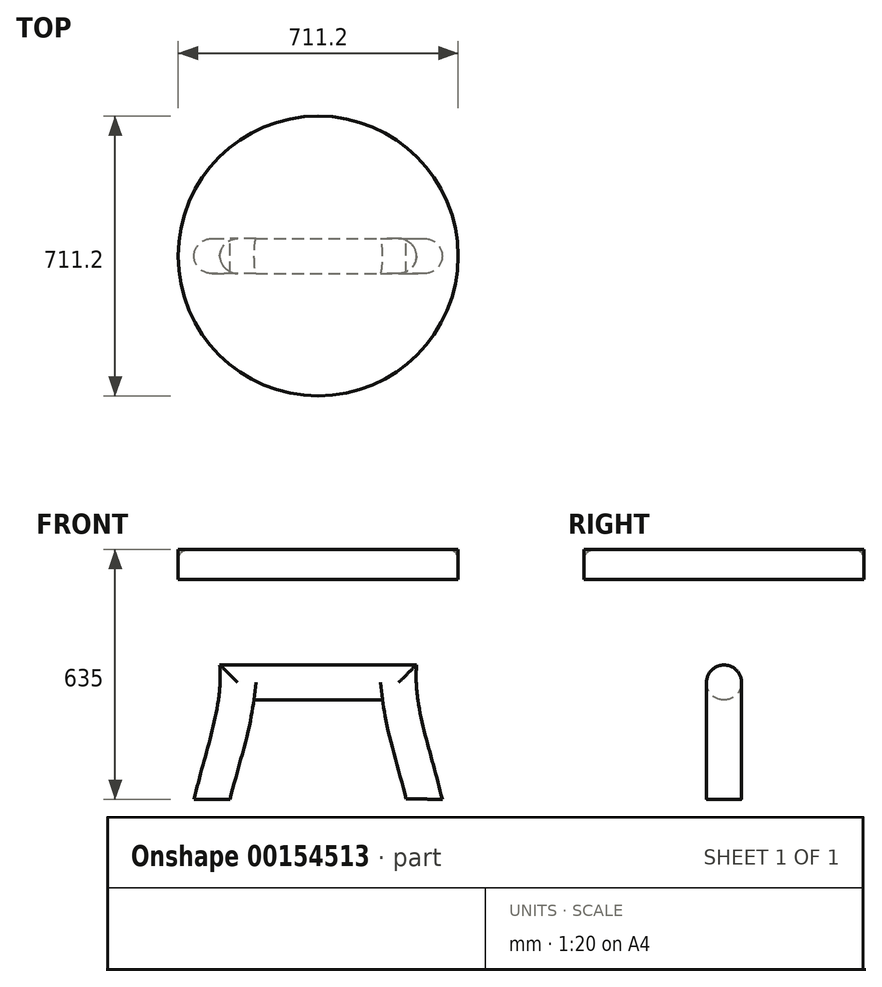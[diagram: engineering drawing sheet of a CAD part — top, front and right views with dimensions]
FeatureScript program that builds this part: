
annotation { "Feature Type Name" : "Feature", "Feature Type Description" : "" }
export const myFeature = defineFeature(function(context is Context, id is Id, definition is map)
    precondition{}
    {
        {
            var Q0;
            Q0=qCreatedBy(makeId("Top.planeOp"),FACE);
            var sketch = newSketch(context, id + "F0", { "sketchPlane" : qUnion([Q0])});
            skCircle(sketch, "E0", {"center": v(0, 0) * mm, "radius": 355.6 * mm});
            skSolve(sketch);
        }
        {
            var Q0;
            Q0=makeQuery(id+"F0.imprint","IMPRINT",FACE,{"disambiguationData":[TD([[makeQuery(id+"F0.imprint","IMPRINT",EDGE,{"derivedFrom":sQuery(id+"F0.wireOp",EDGE,"E0")}),1.0]])]});
            extrude(context, id + "F1", {"entities" : qUnion([Q0]), "oppositeDirection" : true, "depth" : 76.2 * mm});
        }
        {
            var Q0;
            Q0=qCreatedBy(makeId("Front.planeOp"),FACE);
            var sketch = newSketch(context, id + "F2", { "sketchPlane" : qUnion([Q0])});
            skFitSpline(sketch, "E1", {"points": [v(-350.08, -37.61) * mm, v(-250, -293.53) * mm, v(-315.3, -635) * mm], "startDerivative": vector(306.3, -378.15) * mm, "endDerivative": vector(-196.23, -818.74) * mm});
            skLineSegment(sketch, "E2", {"start": v(-315.3, -635) * mm, "end": v(-223.77, -635) * mm});
            skFitSpline(sketch, "E3.0", {"points": [v(-281, 18.35) * mm, v(-276.82, 13.2) * mm, v(-268.7, 2.6) * mm, v(-257.06, -14.11) * mm, v(-245.96, -31.62) * mm, v(-231.83, -55.95) * mm, v(-215.44, -88.12) * mm, v(-200.93, -122.28) * mm, v(-190.63, -150.57) * mm, v(-183.6, -172.21) * mm, v(-177.33, -194.23) * mm, v(-171.89, -216.57) * mm, v(-168.1, -235.43) * mm, v(-165.57, -250.63) * mm, v(-163.92, -262.08) * mm, v(-162.77, -271.67) * mm, v(-162, -279.36) * mm, v(-161.48, -285.15) * mm, v(-161.04, -290.93) * mm, v(-160.68, -296.7) * mm, v(-160.4, -302.43) * mm, v(-160.12, -310.05) * mm, v(-159.94, -319.52) * mm, v(-160.02, -330.79) * mm, v(-160.35, -341.95) * mm, v(-161.14, -356.72) * mm, v(-162.7, -374.92) * mm, v(-165.43, -396.41) * mm, v(-168.87, -417.58) * mm, v(-174.27, -445.47) * mm, v(-182.29, -479.9) * mm, v(-193.22, -521.32) * mm, v(-204.93, -563.73) * mm, v(-216.97, -608.02) * mm, v(-224.94, -639.41) * mm, v(-228.85, -655.72) * mm]});
            skLineSegment(sketch, "E4", {"start": v(0, 0) * mm, "end": v(0, -373.88) * mm, "construction": true});
            skFitSpline(sketch, "E5.MirrorCS", {"points": [v(350.08, -37.61) * mm, v(250, -293.53) * mm, v(315.3, -635) * mm], "startDerivative": vector(-306.3, -378.15) * mm, "endDerivative": vector(196.23, -818.74) * mm});
            skFitSpline(sketch, "E6.0", {"points": [v(281, 18.35) * mm, v(276.82, 13.2) * mm, v(268.7, 2.6) * mm, v(257.06, -14.11) * mm, v(245.96, -31.62) * mm, v(231.83, -55.95) * mm, v(215.44, -88.12) * mm, v(200.93, -122.28) * mm, v(190.63, -150.57) * mm, v(183.6, -172.21) * mm, v(177.33, -194.23) * mm, v(171.89, -216.57) * mm, v(168.1, -235.43) * mm, v(165.57, -250.63) * mm, v(163.92, -262.08) * mm, v(162.77, -271.67) * mm, v(162, -279.36) * mm, v(161.48, -285.15) * mm, v(161.04, -290.93) * mm, v(160.68, -296.7) * mm, v(160.4, -302.43) * mm, v(160.12, -310.05) * mm, v(159.94, -319.52) * mm, v(160.02, -330.79) * mm, v(160.35, -341.95) * mm, v(161.14, -356.72) * mm, v(162.7, -374.92) * mm, v(165.43, -396.41) * mm, v(168.87, -417.58) * mm, v(174.27, -445.47) * mm, v(182.29, -479.9) * mm, v(193.22, -521.32) * mm, v(204.93, -563.73) * mm, v(216.97, -608.02) * mm, v(224.94, -639.41) * mm, v(228.85, -655.72) * mm]});
            skLineSegment(sketch, "E7", {"start": v(-350.08, -37.61) * mm, "end": v(-242.53, -37.61) * mm});
            skLineSegment(sketch, "E8", {"start": v(350.08, -37.61) * mm, "end": v(242.53, -37.61) * mm});
            skLineSegment(sketch, "E9", {"start": v(250, -293.53) * mm, "end": v(-250, -293.53) * mm});
            skLineSegment(sketch, "E10", {"start": v(253.36, -382.43) * mm, "end": v(-253.36, -382.43) * mm});
            skLineSegment(sketch, "E11", {"start": v(223.32, -633.2) * mm, "end": v(315.3, -635) * mm});
            skSolve(sketch);
        }
        {
            var Q0;
            {var subQ0=sQuery(id+"F2.wireOp",EDGE,"E7");var subQ1=sQuery(id+"F2.wireOp",EDGE,"E1");var subQ2=makeQuery(id+"F2.imprint","INTERSECT",VERTEX,{"derivedFrom":[subQ1,subQ0]});Q0=makeQuery(id+"F2.imprint","IMPRINT",FACE,{"disambiguationData":[TD([[makeQuery(id+"F2.imprint","IMPRINT",EDGE,{"disambiguationData":[TD([[subQ2,-1.0]])],"derivedFrom":subQ1}),1.0]])]});}
            var Q1;
            {var subQ0=sQuery(id+"F2.wireOp",EDGE,"E9");var subQ1=sQuery(id+"F2.wireOp",EDGE,"E1");var subQ2=makeQuery(id+"F2.imprint","INTERSECT",VERTEX,{"derivedFrom":[subQ1,subQ0]});Q1=makeQuery(id+"F2.imprint","IMPRINT",FACE,{"disambiguationData":[TD([[makeQuery(id+"F2.imprint","IMPRINT",EDGE,{"disambiguationData":[TD([[subQ2,-1.0]])],"derivedFrom":subQ1}),1.0]])]});}
            var Q2;
            {var subQ0=sQuery(id+"F2.wireOp",EDGE,"E10");var subQ1=sQuery(id+"F2.wireOp",EDGE,"E3.0");var subQ2=makeQuery(id+"F2.imprint","INTERSECT",VERTEX,{"derivedFrom":[subQ1,subQ0]});Q2=makeQuery(id+"F2.imprint","IMPRINT",FACE,{"disambiguationData":[TD([[makeQuery(id+"F2.imprint","IMPRINT",EDGE,{"disambiguationData":[TD([[subQ2,1.0]])],"derivedFrom":subQ1}),1.0]])]});}
            var Q3;
            {var subQ0=sQuery(id+"F2.wireOp",EDGE,"E8");var subQ1=sQuery(id+"F2.wireOp",EDGE,"E5.MirrorCS");var subQ2=makeQuery(id+"F2.imprint","INTERSECT",VERTEX,{"derivedFrom":[subQ1,subQ0]});Q3=makeQuery(id+"F2.imprint","IMPRINT",FACE,{"disambiguationData":[TD([[makeQuery(id+"F2.imprint","IMPRINT",EDGE,{"disambiguationData":[TD([[subQ2,-1.0]])],"derivedFrom":subQ1}),-1.0]])]});}
            var Q4;
            {var subQ0=sQuery(id+"F2.wireOp",EDGE,"E9");var subQ1=sQuery(id+"F2.wireOp",EDGE,"E5.MirrorCS");var subQ2=makeQuery(id+"F2.imprint","INTERSECT",VERTEX,{"derivedFrom":[subQ1,subQ0]});Q4=makeQuery(id+"F2.imprint","IMPRINT",FACE,{"disambiguationData":[TD([[makeQuery(id+"F2.imprint","IMPRINT",EDGE,{"disambiguationData":[TD([[subQ2,-1.0]])],"derivedFrom":subQ1}),-1.0]])]});}
            var Q5;
            {var subQ0=sQuery(id+"F2.wireOp",EDGE,"E2");Q5=makeQuery(id+"F2.imprint","IMPRINT",FACE,{"disambiguationData":[TD([[makeQuery(id+"F2.imprint","IMPRINT",EDGE,{"derivedFrom":subQ0}),1.0]])]});}
            var Q6;
            {var subQ0=sQuery(id+"F2.wireOp",EDGE,"E11");var subQ1=sQuery(id+"F2.wireOp",EDGE,"E5.MirrorCS");var subQ2=makeQuery(id+"F2.imprint","INTERSECT",VERTEX,{"derivedFrom":[subQ1,subQ0]});Q6=makeQuery(id+"F2.imprint","IMPRINT",FACE,{"disambiguationData":[TD([[makeQuery(id+"F2.imprint","IMPRINT",EDGE,{"disambiguationData":[TD([[subQ2,1.0]])],"derivedFrom":subQ1}),-1.0]])]});}
            extrude(context, id + "F3", {"entities" : qUnion([Q0, Q1, Q2, Q3, Q4, Q5, Q6]), "operationType" : NewBodyOperationType.ADD, "depth" : 88.9 * mm, "symmetric" : true});
        }
        {
            var Q0;
            Q0=makeQuery(id+"F1.opExtrude","SWEPT_BODY",BODY,{"disambiguationData":[OSD([sQuery(id+"F0.wireOp",EDGE,"E0")])]});
            var Q1;
            Q1=makeQuery(id+"F1.opExtrude","CAP_EDGE",EDGE,{"disambiguationData":[OSD([sQuery(id+"F0.wireOp",EDGE,"E0")])],"isStart":true});
            circularPattern(context, id + "F4", {"operationType" : NewBodyOperationType.ADD, "entities" : qUnion([Q0]), "axis" : qUnion([Q1]), "angle" : 90 * degree, "instanceCount" : 2});
        }
        {
            var Q0;
            Q0=makeQuery(id+"F4.opPattern","COPY",EDGE,{"derivedFrom":makeQuery(id+"F3.opExtrude","CAP_EDGE",EDGE,{"disambiguationData":[OSD([sQuery(id+"F2.wireOp",EDGE,"E1")])],"isStart":false}),"instanceName":"1"});
            var Q1;
            Q1=makeQuery(id+"F4.opPattern","COPY",EDGE,{"derivedFrom":makeQuery(id+"F3.opExtrude","CAP_EDGE",EDGE,{"disambiguationData":[OSD([sQuery(id+"F2.wireOp",EDGE,"E1")])],"isStart":true}),"instanceName":"1"});
            var Q2;
            Q2=makeQuery(id+"F3.opExtrude","CAP_EDGE",EDGE,{"disambiguationData":[OSD([sQuery(id+"F2.wireOp",EDGE,"E5.MirrorCS")])],"isStart":false});
            var Q3;
            Q3=makeQuery(id+"F3.opExtrude","CAP_EDGE",EDGE,{"disambiguationData":[OSD([sQuery(id+"F2.wireOp",EDGE,"E5.MirrorCS")])],"isStart":true});
            var Q4;
            Q4=makeQuery(id+"F3.opExtrude","CAP_EDGE",EDGE,{"disambiguationData":[OSD([sQuery(id+"F2.wireOp",EDGE,"E1")])],"isStart":false});
            var Q5;
            Q5=makeQuery(id+"F3.opExtrude","CAP_EDGE",EDGE,{"disambiguationData":[OSD([sQuery(id+"F2.wireOp",EDGE,"E1")])],"isStart":true});
            var Q6;
            Q6=makeQuery(id+"F4.opPattern","COPY",EDGE,{"derivedFrom":makeQuery(id+"F3.opExtrude","CAP_EDGE",EDGE,{"disambiguationData":[OSD([sQuery(id+"F2.wireOp",EDGE,"E5.MirrorCS")])],"isStart":true}),"instanceName":"1"});
            var Q7;
            Q7=makeQuery(id+"F4.opPattern","COPY",EDGE,{"derivedFrom":makeQuery(id+"F3.opExtrude","CAP_EDGE",EDGE,{"disambiguationData":[OSD([sQuery(id+"F2.wireOp",EDGE,"E5.MirrorCS")])],"isStart":false}),"instanceName":"1"});
            var Q8;
            {var subQ0=makeQuery(id+"F3.opExtrude","CAP_FACE",FACE,{"disambiguationData":[OSD([sQuery(id+"F2.wireOp",EDGE,"E1"),sQuery(id+"F2.wireOp",EDGE,"E2"),sQuery(id+"F2.wireOp",EDGE,"E3.0"),sQuery(id+"F2.wireOp",EDGE,"E5.MirrorCS"),sQuery(id+"F2.wireOp",EDGE,"E6.0"),sQuery(id+"F2.wireOp",EDGE,"E7"),sQuery(id+"F2.wireOp",EDGE,"E8"),sQuery(id+"F2.wireOp",EDGE,"E9"),sQuery(id+"F2.wireOp",EDGE,"E10"),sQuery(id+"F2.wireOp",EDGE,"E11")])],"isStart":false});Q8=makeQuery(id+"F4.boolean.opBoolean","INTERSECT",EDGE,{"derivedFrom":[subQ0,makeQuery(id+"F4.opPattern","COPY",FACE,{"derivedFrom":subQ0,"instanceName":"1"})]});}
            var Q9;
            {var subQ0=sQuery(id+"F2.wireOp",EDGE,"E11");var subQ1=sQuery(id+"F2.wireOp",EDGE,"E10");var subQ2=sQuery(id+"F2.wireOp",EDGE,"E9");var subQ3=sQuery(id+"F2.wireOp",EDGE,"E8");var subQ4=sQuery(id+"F2.wireOp",EDGE,"E7");var subQ5=sQuery(id+"F2.wireOp",EDGE,"E6.0");var subQ6=sQuery(id+"F2.wireOp",EDGE,"E5.MirrorCS");var subQ7=sQuery(id+"F2.wireOp",EDGE,"E3.0");var subQ8=sQuery(id+"F2.wireOp",EDGE,"E2");var subQ9=sQuery(id+"F2.wireOp",EDGE,"E1");Q9=makeQuery(id+"F4.boolean.opBoolean","INTERSECT",EDGE,{"derivedFrom":[makeQuery(id+"F3.opExtrude","CAP_FACE",FACE,{"disambiguationData":[OSD([subQ9,subQ8,subQ7,subQ6,subQ5,subQ4,subQ3,subQ2,subQ1,subQ0])],"isStart":false}),makeQuery(id+"F4.opPattern","COPY",FACE,{"derivedFrom":makeQuery(id+"F3.opExtrude","CAP_FACE",FACE,{"disambiguationData":[OSD([subQ9,subQ8,subQ7,subQ6,subQ5,subQ4,subQ3,subQ2,subQ1,subQ0])],"isStart":true}),"instanceName":"1"})]});}
            var Q10;
            {var subQ0=makeQuery(id+"F3.opExtrude","CAP_FACE",FACE,{"disambiguationData":[OSD([sQuery(id+"F2.wireOp",EDGE,"E1"),sQuery(id+"F2.wireOp",EDGE,"E2"),sQuery(id+"F2.wireOp",EDGE,"E3.0"),sQuery(id+"F2.wireOp",EDGE,"E5.MirrorCS"),sQuery(id+"F2.wireOp",EDGE,"E6.0"),sQuery(id+"F2.wireOp",EDGE,"E7"),sQuery(id+"F2.wireOp",EDGE,"E8"),sQuery(id+"F2.wireOp",EDGE,"E9"),sQuery(id+"F2.wireOp",EDGE,"E10"),sQuery(id+"F2.wireOp",EDGE,"E11")])],"isStart":true});Q10=makeQuery(id+"F4.boolean.opBoolean","INTERSECT",EDGE,{"derivedFrom":[subQ0,makeQuery(id+"F4.opPattern","COPY",FACE,{"derivedFrom":subQ0,"instanceName":"1"})]});}
            var Q11;
            {var subQ0=sQuery(id+"F2.wireOp",EDGE,"E11");var subQ1=sQuery(id+"F2.wireOp",EDGE,"E10");var subQ2=sQuery(id+"F2.wireOp",EDGE,"E9");var subQ3=sQuery(id+"F2.wireOp",EDGE,"E8");var subQ4=sQuery(id+"F2.wireOp",EDGE,"E7");var subQ5=sQuery(id+"F2.wireOp",EDGE,"E6.0");var subQ6=sQuery(id+"F2.wireOp",EDGE,"E5.MirrorCS");var subQ7=sQuery(id+"F2.wireOp",EDGE,"E3.0");var subQ8=sQuery(id+"F2.wireOp",EDGE,"E2");var subQ9=sQuery(id+"F2.wireOp",EDGE,"E1");Q11=makeQuery(id+"F4.boolean.opBoolean","INTERSECT",EDGE,{"derivedFrom":[makeQuery(id+"F3.opExtrude","CAP_FACE",FACE,{"disambiguationData":[OSD([subQ9,subQ8,subQ7,subQ6,subQ5,subQ4,subQ3,subQ2,subQ1,subQ0])],"isStart":true}),makeQuery(id+"F4.opPattern","COPY",FACE,{"derivedFrom":makeQuery(id+"F3.opExtrude","CAP_FACE",FACE,{"disambiguationData":[OSD([subQ9,subQ8,subQ7,subQ6,subQ5,subQ4,subQ3,subQ2,subQ1,subQ0])],"isStart":false}),"instanceName":"1"})]});}
            var Q12;
            {var subQ0=sQuery(id+"F2.wireOp",EDGE,"E9");var subQ2=sQuery(id+"F2.wireOp",EDGE,"E8");var subQ3=sQuery(id+"F2.wireOp",EDGE,"E6.0");Q12=makeQuery(id+"F4.boolean.opBoolean","SPLIT",EDGE,{"disambiguationData":[TD([makeQuery(id+"F3.opExtrude","SWEPT_FACE",FACE,{"disambiguationData":[OSD([subQ3]),TDD([makeQuery(id+"F2.imprint","IMPRINT",EDGE,{"disambiguationData":[TD([[makeQuery(id+"F2.imprint","INTERSECT",VERTEX,{"derivedFrom":[subQ3,subQ2]}),-1.0]])],"derivedFrom":subQ3})])]})])],"derivedFrom":makeQuery(id+"F3.opExtrude","CAP_EDGE",EDGE,{"disambiguationData":[OSD([subQ0])],"isStart":true})});}
            var Q13;
            {var subQ0=sQuery(id+"F2.wireOp",EDGE,"E9");var subQ2=sQuery(id+"F2.wireOp",EDGE,"E8");var subQ3=sQuery(id+"F2.wireOp",EDGE,"E6.0");Q13=makeQuery(id+"F4.boolean.opBoolean","SPLIT",EDGE,{"disambiguationData":[TD([makeQuery(id+"F3.opExtrude","SWEPT_FACE",FACE,{"disambiguationData":[OSD([subQ3]),TDD([makeQuery(id+"F2.imprint","IMPRINT",EDGE,{"disambiguationData":[TD([[makeQuery(id+"F2.imprint","INTERSECT",VERTEX,{"derivedFrom":[subQ3,subQ2]}),-1.0]])],"derivedFrom":subQ3})])]})])],"derivedFrom":makeQuery(id+"F3.opExtrude","CAP_EDGE",EDGE,{"disambiguationData":[OSD([subQ0])],"isStart":false})});}
            var Q14;
            {var subQ0=sQuery(id+"F2.wireOp",EDGE,"E9");var subQ2=sQuery(id+"F2.wireOp",EDGE,"E7");var subQ3=sQuery(id+"F2.wireOp",EDGE,"E3.0");Q14=makeQuery(id+"F4.boolean.opBoolean","SPLIT",EDGE,{"disambiguationData":[TD([makeQuery(id+"F3.opExtrude","SWEPT_FACE",FACE,{"disambiguationData":[OSD([subQ3]),TDD([makeQuery(id+"F2.imprint","IMPRINT",EDGE,{"disambiguationData":[TD([[makeQuery(id+"F2.imprint","INTERSECT",VERTEX,{"derivedFrom":[subQ3,subQ2]}),-1.0]])],"derivedFrom":subQ3})])]})])],"derivedFrom":makeQuery(id+"F3.opExtrude","CAP_EDGE",EDGE,{"disambiguationData":[OSD([subQ0])],"isStart":true})});}
            var Q15;
            {var subQ2=sQuery(id+"F2.wireOp",EDGE,"E9");var subQ4=sQuery(id+"F2.wireOp",EDGE,"E7");var subQ7=sQuery(id+"F2.wireOp",EDGE,"E3.0");Q15=makeQuery(id+"F4.boolean.opBoolean","SPLIT",EDGE,{"disambiguationData":[TD([makeQuery(id+"F4.opPattern","COPY",FACE,{"derivedFrom":makeQuery(id+"F3.opExtrude","SWEPT_FACE",FACE,{"disambiguationData":[OSD([subQ7]),TDD([makeQuery(id+"F2.imprint","IMPRINT",EDGE,{"disambiguationData":[TD([[makeQuery(id+"F2.imprint","INTERSECT",VERTEX,{"derivedFrom":[subQ7,subQ4]}),-1.0]])],"derivedFrom":subQ7})])]}),"instanceName":"1"})])],"derivedFrom":makeQuery(id+"F4.opPattern","COPY",EDGE,{"derivedFrom":makeQuery(id+"F3.opExtrude","CAP_EDGE",EDGE,{"disambiguationData":[OSD([subQ2])],"isStart":true}),"instanceName":"1"})});}
            var Q16;
            {var subQ0=sQuery(id+"F2.wireOp",EDGE,"E10");var subQ2=sQuery(id+"F2.wireOp",EDGE,"E11");var subQ3=sQuery(id+"F2.wireOp",EDGE,"E6.0");Q16=makeQuery(id+"F4.boolean.opBoolean","SPLIT",EDGE,{"disambiguationData":[TD([makeQuery(id+"F4.opPattern","COPY",FACE,{"derivedFrom":makeQuery(id+"F3.opExtrude","SWEPT_FACE",FACE,{"disambiguationData":[OSD([subQ3]),TDD([makeQuery(id+"F2.imprint","IMPRINT",EDGE,{"disambiguationData":[TD([[makeQuery(id+"F2.imprint","INTERSECT",VERTEX,{"derivedFrom":[subQ3,subQ2]}),1.0]])],"derivedFrom":subQ3})])]}),"instanceName":"1"})])],"derivedFrom":makeQuery(id+"F4.opPattern","COPY",EDGE,{"derivedFrom":makeQuery(id+"F3.opExtrude","CAP_EDGE",EDGE,{"disambiguationData":[OSD([subQ0])],"isStart":true}),"instanceName":"1"})});}
            var Q17;
            {var subQ0=sQuery(id+"F2.wireOp",EDGE,"E10");var subQ8=sQuery(id+"F2.wireOp",EDGE,"E3.0");var subQ9=sQuery(id+"F2.wireOp",EDGE,"E2");Q17=makeQuery(id+"F4.boolean.opBoolean","SPLIT",EDGE,{"disambiguationData":[TD([makeQuery(id+"F3.opExtrude","SWEPT_FACE",FACE,{"disambiguationData":[OSD([subQ8]),TDD([makeQuery(id+"F2.imprint","IMPRINT",EDGE,{"disambiguationData":[TD([[makeQuery(id+"F2.imprint","INTERSECT",VERTEX,{"derivedFrom":[subQ9,subQ8]}),1.0]])],"derivedFrom":subQ8})])]})])],"derivedFrom":makeQuery(id+"F3.opExtrude","CAP_EDGE",EDGE,{"disambiguationData":[OSD([subQ0])],"isStart":false})});}
            var Q18;
            {var subQ0=sQuery(id+"F2.wireOp",EDGE,"E10");var subQ2=sQuery(id+"F2.wireOp",EDGE,"E11");var subQ3=sQuery(id+"F2.wireOp",EDGE,"E6.0");Q18=makeQuery(id+"F4.boolean.opBoolean","SPLIT",EDGE,{"disambiguationData":[TD([makeQuery(id+"F3.opExtrude","SWEPT_FACE",FACE,{"disambiguationData":[OSD([subQ3]),TDD([makeQuery(id+"F2.imprint","IMPRINT",EDGE,{"disambiguationData":[TD([[makeQuery(id+"F2.imprint","INTERSECT",VERTEX,{"derivedFrom":[subQ3,subQ2]}),1.0]])],"derivedFrom":subQ3})])]})])],"derivedFrom":makeQuery(id+"F3.opExtrude","CAP_EDGE",EDGE,{"disambiguationData":[OSD([subQ0])],"isStart":false})});}
            var Q19;
            {var subQ0=sQuery(id+"F2.wireOp",EDGE,"E10");var subQ2=sQuery(id+"F2.wireOp",EDGE,"E11");var subQ3=sQuery(id+"F2.wireOp",EDGE,"E6.0");Q19=makeQuery(id+"F4.boolean.opBoolean","SPLIT",EDGE,{"disambiguationData":[TD([makeQuery(id+"F3.opExtrude","SWEPT_FACE",FACE,{"disambiguationData":[OSD([subQ3]),TDD([makeQuery(id+"F2.imprint","IMPRINT",EDGE,{"disambiguationData":[TD([[makeQuery(id+"F2.imprint","INTERSECT",VERTEX,{"derivedFrom":[subQ3,subQ2]}),1.0]])],"derivedFrom":subQ3})])]})])],"derivedFrom":makeQuery(id+"F3.opExtrude","CAP_EDGE",EDGE,{"disambiguationData":[OSD([subQ0])],"isStart":true})});}
            fillet(context, id + "F5", {"entities" : qUnion([Q0, Q1, Q2, Q3, Q4, Q5, Q6, Q7, Q8, Q9, Q10, Q11, Q12, Q13, Q14, Q15, Q16, Q17, Q18, Q19]), "radius" : 44.45 * mm, "tangentPropagation" : true, "allowEdgeOverflow" : false});
        }
        {
            var Q0;
            Q0=makeQuery(id+"F1.opExtrude","CAP_FACE",FACE,{"disambiguationData":[OSD([sQuery(id+"F0.wireOp",EDGE,"E0")])],"isStart":true});
            fillet(context, id + "F6", {"entities" : qUnion([Q0]), "radius" : 25.4 * mm, "tangentPropagation" : true, "allowEdgeOverflow" : false});
        }
    });
